# Revit family: Thermostatic_Trim-Grohe-Atrio_New-24151XXX_Series
name_source: partatom
category: Plumbing Fixtures
units: mm (PartAtom-declared; Revit-internal decimal feet)

## family parameters
Cut with Voids When Loaded = No
Host = Face
OmniClass Number = 23.45.05.14.17
OmniClass Title = Showers
Part Type = Normal
Room Calculation Point = No
Round Connector Dimension = Use Diameter
Shared = Yes

## types (2) — shared parameters
Assembly Code = D2010710
CEC Compliant = Yes
CW Connection = No
Default Elevation = 40"
Description = Atrio® New Dual Function 2-Handle Thermostatic Valve Trim
HW Connection = No
Height = 6 1/4"
IAPMO Compliance = ASME A112.18.1/CSA B125.1
Installation Type = Wall Mounted
Length = 1 11/16"
Manufacturer = Grohe
Price = Prices may vary. Please consult Manufacturer Representative for most up-to-date price list.
Product Documentation Link = https://americanstandard.box.com
Product Page URL = https://www.grohe.us
URL = https://www.grohe.com
Vent Connection = No
Warranty Documentation Link = https://cdn.cloud.grohe.com
Warranty Information = Limited Lifetime Warranty
Waste Connection = No
Width = 6 1/4"
zero-valued in all types: CWFU, HWFU, WFU

## per-type parameters (varying)
| type | Finish | Material |
| 24151003 | Metal-Grohe-001-StarLightChrome | Metal-Grohe-001-StarLight_Chrome |
| 24151EN3 | Metal-Grohe-EN3-Brushed Nickel | Metal-Grohe-EN3-Brushed Nickel |

note: column(s) folded — value = type name in every type: Model

## geometry (parser evidence)
native form markers: Sweep x2
no freeform markers — native parametric forms only
